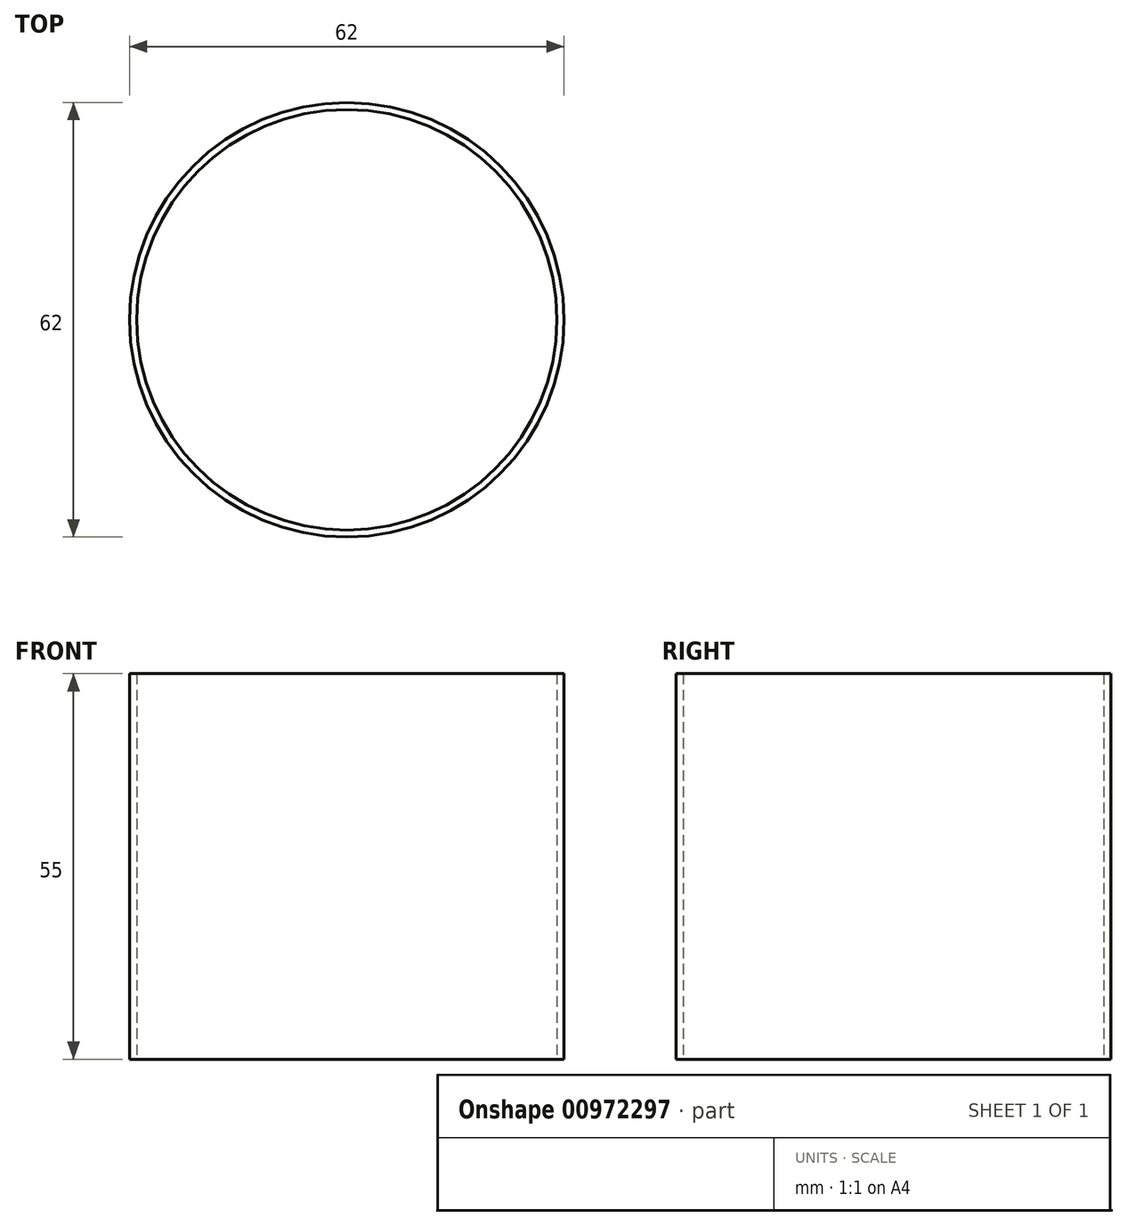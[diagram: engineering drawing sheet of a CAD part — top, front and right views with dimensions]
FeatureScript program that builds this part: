
annotation { "Feature Type Name" : "Feature", "Feature Type Description" : "" }
export const myFeature = defineFeature(function(context is Context, id is Id, definition is map)
    precondition{}
    {
        {
            var Q0;
            Q0=qCreatedBy(makeId("Top.planeOp"),FACE);
            var sketch = newSketch(context, id + "F0", { "sketchPlane" : qUnion([Q0])});
            skCircle(sketch, "E0", {"center": v(0, 0) * mm, "radius": 30 * mm});
            skCircle(sketch, "E1.0", {"center": v(0, 0) * mm, "radius": 31 * mm});
            skSolve(sketch);
        }
        {
            var Q0;
            Q0=makeQuery(id+"F0.imprint","IMPRINT",FACE,{"disambiguationData":[TD([[makeQuery(id+"F0.imprint","IMPRINT",EDGE,{"derivedFrom":sQuery(id+"F0.wireOp",EDGE,"E0")}),-1.0]])]});
            extrude(context, id + "F1", {"entities" : qUnion([Q0]), "depth" : 55 * mm, "offsetDistance" : 25 * mm});
        }
    });
